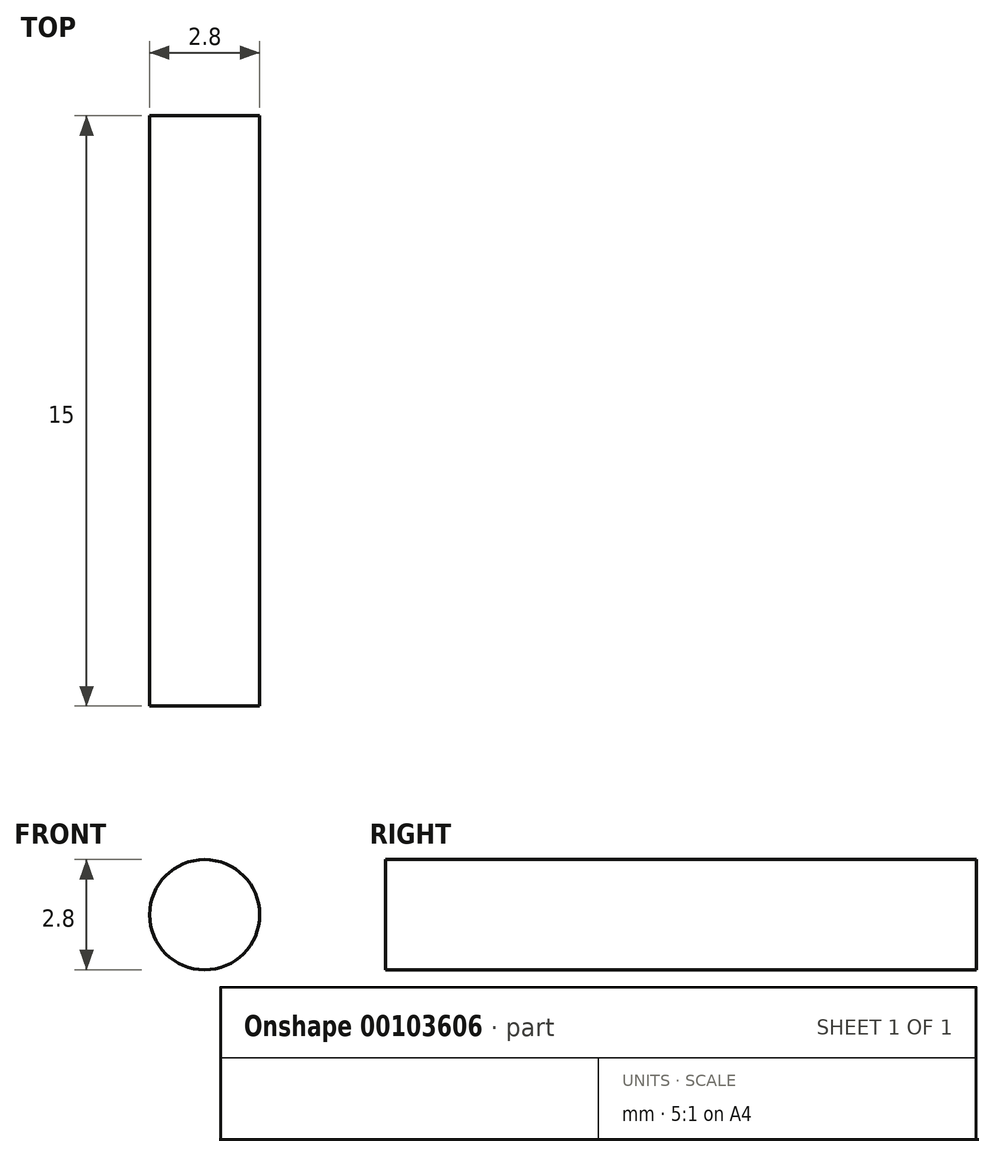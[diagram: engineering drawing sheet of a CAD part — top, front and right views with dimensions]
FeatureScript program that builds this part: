
annotation { "Feature Type Name" : "Feature", "Feature Type Description" : "" }
export const myFeature = defineFeature(function(context is Context, id is Id, definition is map)
    precondition{}
    {
        {
            var Q0;
            Q0=qCreatedBy(makeId("Front.planeOp"),FACE);
            var sketch = newSketch(context, id + "F0", { "sketchPlane" : qUnion([Q0])});
            skCircle(sketch, "E0", {"center": v(0, 0) * mm, "radius": 1.4 * mm});
            skSolve(sketch);
        }
        {
            var Q0;
            Q0=makeQuery(id+"F0.imprint","IMPRINT",FACE,{"disambiguationData":[TD([[makeQuery(id+"F0.imprint","IMPRINT",EDGE,{"derivedFrom":sQuery(id+"F0.wireOp",EDGE,"E0")}),1.0]])]});
            extrude(context, id + "F1", {"entities" : qUnion([Q0]), "depth" : 15 * mm});
        }
    });
